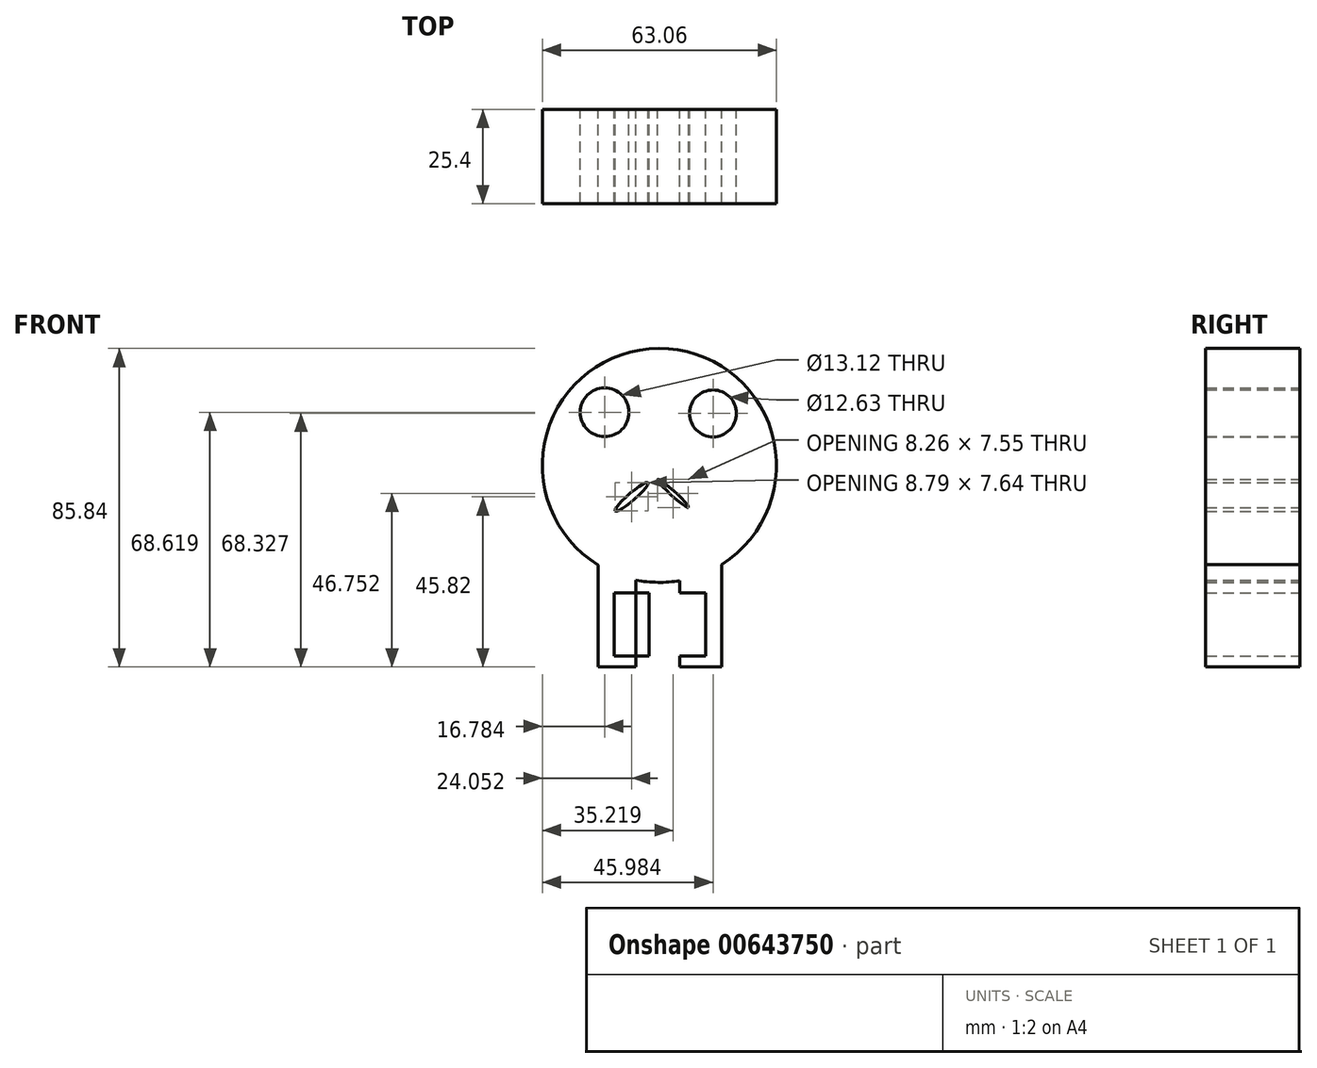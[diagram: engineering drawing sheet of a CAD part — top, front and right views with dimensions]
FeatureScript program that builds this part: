
annotation { "Feature Type Name" : "Feature", "Feature Type Description" : "" }
export const myFeature = defineFeature(function(context is Context, id is Id, definition is map)
    precondition{}
    {
        {
            var Q0;
            Q0=qCreatedBy(makeId("Front.planeOp"),FACE);
            var sketch = newSketch(context, id + "F0", { "sketchPlane" : qUnion([Q0])});
            skCircle(sketch, "E0", {"center": v(0, 34.31) * mm, "radius": 31.53 * mm});
            skCircle(sketch, "E1", {"center": v(-14.75, 48.62) * mm, "radius": 6.56 * mm});
            skCircle(sketch, "E2", {"center": v(14.45, 48.33) * mm, "radius": 6.32 * mm});
            skLineSegment(sketch, "E3", {"start": v(-16.5, 7.44) * mm, "end": v(-16.5, -20) * mm});
            skLineSegment(sketch, "E4", {"start": v(-16.5, -20) * mm, "end": v(16.8, -20) * mm});
            skLineSegment(sketch, "E5", {"start": v(16.8, -20) * mm, "end": v(16.8, 7.62) * mm});
            skEllipse(sketch, "E6", {"center": v(-7.48, 25.82) * mm, "majorRadius": 5.82 * mm, "minorRadius": 1 * mm, "majorAxis": v(-0.75, -0.66)});
            skEllipse(sketch, "E7", {"center": v(3.69, 26.75) * mm, "majorRadius": 5.6 * mm, "minorRadius": 0.63 * mm, "majorAxis": v(0.74, -0.67)});
            skLineSegment(sketch, "E8", {"start": v(-6.34, 3.42) * mm, "end": v(-6.34, -20) * mm});
            skLineSegment(sketch, "E9", {"start": v(5.52, 3.27) * mm, "end": v(5.52, -20) * mm});
            skLineSegment(sketch, "E10.bottom", {"start": v(-12.12, 0) * mm, "end": v(12.41, 0) * mm});
            skLineSegment(sketch, "E10.top", {"start": v(-12.12, -17.08) * mm, "end": v(12.41, -17.08) * mm});
            skLineSegment(sketch, "E10.left", {"start": v(-12.12, 0) * mm, "end": v(-12.12, -17.08) * mm});
            skLineSegment(sketch, "E10.right", {"start": v(12.41, 0) * mm, "end": v(12.41, -17.08) * mm});
            skLineSegment(sketch, "E11.bottom", {"start": v(-2.77, 0) * mm, "end": v(2.77, 0) * mm});
            skLineSegment(sketch, "E11.top", {"start": v(-2.77, -17.08) * mm, "end": v(2.77, -17.08) * mm});
            skLineSegment(sketch, "E11.left", {"start": v(-2.77, 0) * mm, "end": v(-2.77, -17.08) * mm});
            skLineSegment(sketch, "E11.right", {"start": v(2.77, 0) * mm, "end": v(2.77, -17.08) * mm});
            skSolve(sketch);
        }
        {
            var Q0;
            Q0=makeQuery(id+"F0.imprint","IMPRINT",FACE,{"disambiguationData":[TD([[makeQuery(id+"F0.imprint","IMPRINT",EDGE,{"derivedFrom":sQuery(id+"F0.wireOp",EDGE,"E1")}),-1.0]])]});
            var Q1;
            {var subQ0=sQuery(id+"F0.wireOp",EDGE,"E3");Q1=makeQuery(id+"F0.imprint","IMPRINT",FACE,{"disambiguationData":[TD([[makeQuery(id+"F0.imprint","IMPRINT",EDGE,{"derivedFrom":subQ0}),1.0]])]});}
            var Q2;
            {var subQ0=sQuery(id+"F0.wireOp",EDGE,"E8");Q2=makeQuery(id+"F0.imprint","IMPRINT",FACE,{"disambiguationData":[TD([[makeQuery(id+"F0.imprint","IMPRINT",EDGE,{"derivedFrom":subQ0}),1.0]])]});}
            var Q3;
            {var subQ0=sQuery(id+"F0.wireOp",EDGE,"E5");Q3=makeQuery(id+"F0.imprint","IMPRINT",FACE,{"disambiguationData":[TD([[makeQuery(id+"F0.imprint","IMPRINT",EDGE,{"derivedFrom":subQ0}),1.0]])]});}
            extrude(context, id + "F1", {"entities" : qUnion([Q0, Q1, Q2, Q3]), "depth" : 25.4 * mm, "offsetDistance" : 25.4 * mm});
        }
    });
